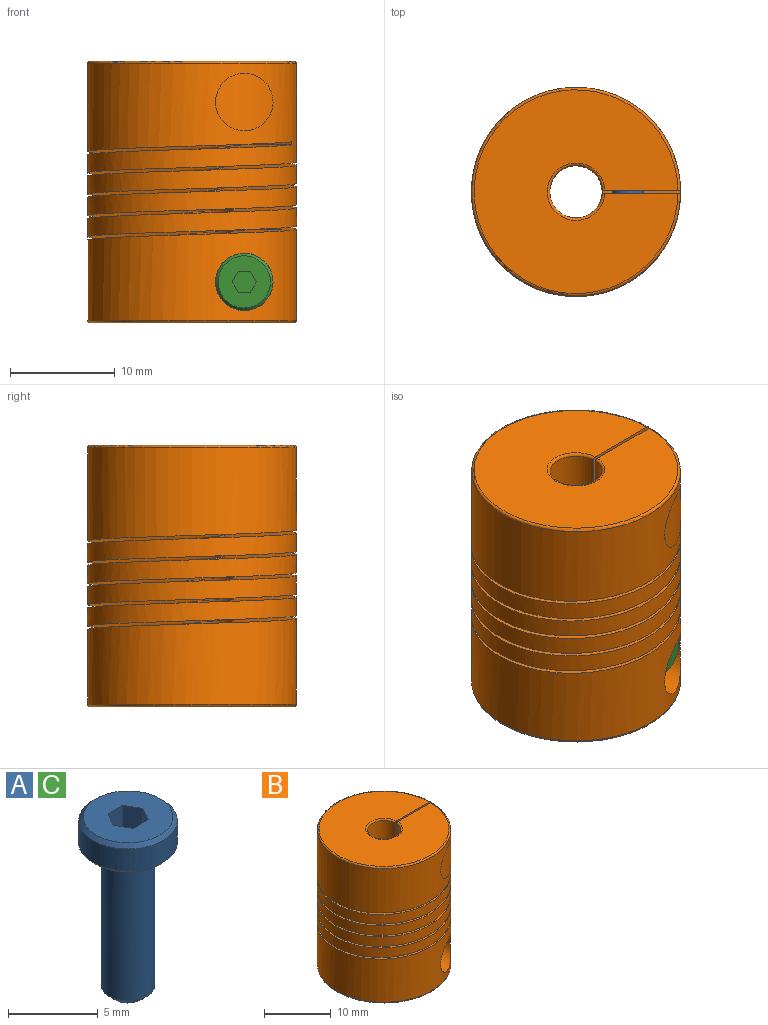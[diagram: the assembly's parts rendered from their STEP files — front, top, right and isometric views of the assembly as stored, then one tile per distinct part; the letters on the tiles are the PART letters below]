
ASSEMBLY  parts=3 mates=2
PART A: 15 faces, bbox 5.5x5.5x12 mm
  f0: plane 5x5mm, normal (0,0,1), area 16.2mm2, adj f3,f4,f5,f6,f7,f8,f11
  f1: cylinder r=2.75mm len=5.5mm, axis (0,0,-1), area 25.9mm2, adj f10,f11
  f2: plane 5x5mm, normal (0,0,-1), area 12.6mm2, adj f10,f12
  f3: plane 1.5x1mm, normal (-0.87,-0.5,0), area 1.7mm2, adj f0,f4,f8,f9
  f4: plane 1.5x1.15mm, normal (0,-1,0), area 1.7mm2, adj f0,f3,f5,f9
  f5: plane 1.5x1mm, normal (0.87,-0.5,0), area 1.7mm2, adj f0,f4,f6,f9
  f6: plane 1.5x1mm, normal (0.87,0.5,0), area 1.7mm2, adj f0,f5,f7,f9
  f7: plane 1.5x1.15mm, normal (0,1,0), area 1.7mm2, adj f0,f6,f8,f9
  f8: plane 1.5x1mm, normal (-0.87,0.5,0), area 1.7mm2, adj f0,f3,f7,f9
  f9: plane 2.31x2mm, normal (0,0,1), area 3.5mm2, adj f3,f4,f5,f6,f7,f8
  f10: cone r=2.75mm half-angle=45deg, axis (0,0,1), area 5.8mm2, adj f1,f2
  f11: cone r=2.5mm half-angle=45deg, axis (0,0,-1), area 5.8mm2, adj f0,f1
  f12: cylinder r=1.5mm len=9.5mm, axis (0,0,1), area 89.5mm2, adj f2,f14
  f13: plane 2x2mm, normal (0,0,-1), area 3.1mm2, adj f14
  f14: cone r=1mm half-angle=45deg, axis (0,0,1), area 5.6mm2, adj f12,f13
PART B: 35 faces, bbox 25.6x25x26.9 mm
  f0: plane 19.5x19.5mm, normal (0,0,1), area 272.8mm2, adj f1,f2,f3,f4
  f1: torus R=2.75mm, axis (0,0,1), area 6.3mm2, adj f0,f2,f4,f5
  f2: plane 10.94x8.69mm, normal (0,-1,0), area 65.1mm2, adj f0,f1,f3,f5,f6,f7,f8,f9
  f3: torus R=9.75mm, axis (0,0,1), area 24.3mm2, adj f0,f2,f4,f8
  f4: plane 11.23x8.98mm, normal (0,1,0), area 65mm2, adj f0,f1,f3,f5,f7,f8,f9,f14
  f5: cylinder r=2.5mm len=12.25mm, axis (0,0,-1), area 189.6mm2, adj f1,f2,f4,f9,f18
  f6: cylinder r=1.5mm len=8.51mm, axis (0,-1,0), area 80.2mm2, adj f2,f8
  f7: bspline ~23.64x23.09mm, area 1338.1mm2, adj f2,f4,f8,f9,f15,f16,f18,f19
  f8: cylinder r=10mm len=24.5mm, axis (0,0,-1), area 1412.2mm2, adj f2,f3,f4,f6,f7,f15,f17,f20
  f9: plane 2.9x0.3mm, normal (0,0,1), area 0.8mm2, adj f2,f4,f5,f7
  f10: bspline ~14.7x14.09mm, area 2.6mm2, adj f2,f11,f13
  f11: cylinder r=3.15mm len=2.4mm, axis (0,0,1), area 0.8mm2, adj f2,f10,f12,f13
  f12: bspline ~14.7x14.09mm, area 2.6mm2, adj f2,f11,f13
  f13: plane 3.31x2.4mm, normal (-0.59,-0.81,0), area 1.2mm2, adj f2,f10,f11,f12
  f14: cylinder r=1.5mm len=4.25mm, axis (0,-1,0), area 40.1mm2, adj f4,f26
  f15: plane 3.97x2.88mm, normal (-0.59,-0.81,0), area 1.5mm2, adj f4,f7,f8,f17
  f16: cylinder r=3.15mm len=6.3mm, axis (0,0,1), area 12.6mm2, adj f4,f7,f17,f18
  f17: bspline ~23.64x23.09mm, area 1094.1mm2, adj f4,f8,f15,f16,f18,f19,f21
  f18: plane 8x7.75mm, normal (0,0,-1), area 27.8mm2, adj f5,f7,f16,f17,f19
  f19: cylinder r=4mm len=12.25mm, axis (0,0,-1), area 278.9mm2, adj f7,f17,f18,f20,f21,f23,f24,f27
  f20: plane 7.03x0.3mm, normal (0,1,0), area 2.1mm2, adj f7,f8,f19,f24
  f21: plane 10.73x7.79mm, normal (0,-1,0), area 47mm2, adj f8,f17,f19,f22,f28,f29,f30
  f22: torus R=9.75mm, axis (0,0,1), area 24.3mm2, adj f8,f21,f23,f30
  f23: plane 10.87x7.94mm, normal (0,1,0), area 46.9mm2, adj f8,f19,f22,f24,f27,f29,f30
  f24: bspline ~23.64x23.09mm, area 239.9mm2, adj f8,f19,f20,f23
  f25: cylinder r=2.75mm len=5.5mm, axis (0,-1,0), area 68.3mm2, adj f8,f31
  f26: plane 5.5x5.5mm, normal (0,-1,0), area 16.7mm2, adj f14,f32
  f27: cylinder r=1.5mm len=4.25mm, axis (0,-1,0), area 36.6mm2, adj f19,f23,f31
  f28: cylinder r=1.5mm len=9.22mm, axis (0,-1,0), area 75.9mm2, adj f19,f21,f33
  f29: torus R=4.25mm, axis (0,0,1), area 10mm2, adj f19,f21,f23,f30
  f30: plane 19.5x19.5mm, normal (0,0,-1), area 240.3mm2, adj f21,f22,f23,f29
  f31: plane 5.5x5.5mm, normal (0,-1,0), area 16.7mm2, adj f25,f27
  f32: cylinder r=2.75mm len=5.5mm, axis (0,-1,0), area 68.3mm2, adj f26,f34
  f33: cylinder r=10mm len=3mm, axis (0,0,-1), area 8.2mm2, adj f28
  f34: cylinder r=10mm len=5.5mm, axis (0,0,-1), area 28.2mm2, adj f32
PART C: same geometry as A
PLACE A rot(axis=(1,0,0),90deg) t=(-70.1,9.85,412.6)mm
PLACE B t=(-75.1,14.25,391.5)mm
PLACE C rot(axis=(1,0,0),90deg) t=(-70.1,9.85,395.4)mm
MATE fastened C.f1 <-> B.f25  axis (0,1,0) through (-70.1,9.85,395.4)mm
MATE fastened A.f1 <-> B.f6  axis (0,1,0) through (-70.1,9.85,412.6)mm
